# Revit family: 10. Водяные нагреватели UTR GLP
name_source: partatom
category: Оборудование
revit_build: Autodesk Revit 2016 (Build: 20161004_0715(x64)
units: mm (PartAtom-declared; Revit-internal decimal feet)

## family parameters
Всегда вертикально = Да
На основе рабочей плоскости = Нет
Общий = Нет
При загрузке вырезать с полостями = Нет
Размер круглого соединителя = Использовать диаметр
Тип детали = Нормальный
Точка расчета площади = Нет

## types (8) — shared parameters
h = 60 мм
Д = 350 мм
Д1 = 330 мм
Единица измерения = шт.
Завод изготовитель = KORF
Ключевая пометка = Вентиляция
Материал = Сталь серая
Наименование и тех.хар-ка = Рекуператор с промежуточным теплоносителем - приточная секция
Раздел = ОВ
Синий = Синий
высота ножек = 50 мм

## per-type parameters (varying)
| type | d | А | А1 | Б | Б1 | Г | Заправочный объем, л | Масса единицы | Теплопроизводительность, кВт | Тип, марка, обозначение | высота | размер В | ширина |
| 50-25 | 32 мм | 710 мм | 690 мм | 470 мм | 450 мм | 395 мм | 1 м³ | 36 | 26 кВт | UTR 50-25 GLP | 250 мм | 635 мм | 500 мм |
| 50-30 | 38 мм | 710 мм | 690 мм | 520 мм | 500 мм | 445 мм | 1.3 м³ | 38 | 31 кВт | UTR 50-30 GLP | 300 мм | 635 мм | 500 мм |
| 60-30 | 38 мм | 810 мм | 790 мм | 520 мм | 500 мм | 445 мм | 1.5 м³ | 42 | 37 кВт | UTR 60-30 GLP | 300 мм | 735 мм | 600 мм |
| 60-35 | 51 мм | 810 мм | 790 мм | 570 мм | 550 мм | 495 мм | 1.7 м³ | 46 | 44 кВт | UTR 60-35 GLP | 350 мм | 735 мм | 600 мм |
| 70-40 | 51 мм | 910 мм | 890 мм | 620 мм | 600 мм | 545 мм | 2.2 м³ | 54 | 59 кВт | UTR 70-40 GLP | 400 мм | 835 мм | 700 мм |
| 80-50 | 51 мм | 1010 мм | 990 мм | 720 мм | 700 мм | 645 мм | 3.2 м³ | 69 | 83 кВт | UTR 80-50 GLP | 500 мм | 935 мм | 800 мм |
| 90-50 | 51 мм | 1125 мм | 1105 мм | 740 мм | 720 мм | 645 мм | 3.5 м³ | 72 | 93 кВт | UTR 90-50 GLP | 500 мм | 1050 мм | 900 мм |
| 100-50 | 51 мм | 1225 мм | 1205 мм | 740 мм | 720 мм | 665 мм | 3.8 м³ | 78 | 102 кВт | UTR 100-50 GLP | 500 мм | 1150 мм | 1000 мм |
